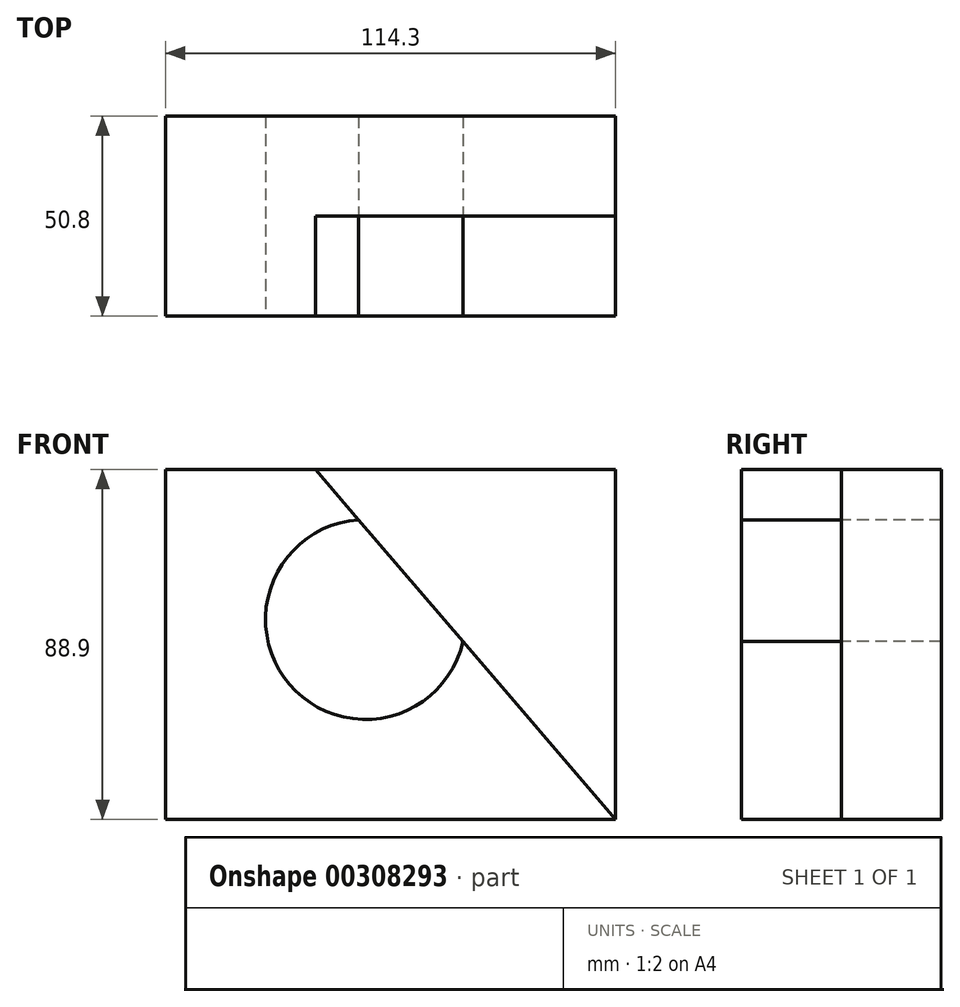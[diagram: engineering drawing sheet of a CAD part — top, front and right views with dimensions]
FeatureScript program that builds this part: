
annotation { "Feature Type Name" : "Feature", "Feature Type Description" : "" }
export const myFeature = defineFeature(function(context is Context, id is Id, definition is map)
    precondition{}
    {
        {
            var Q0;
            Q0=qCreatedBy(makeId("Front.planeOp"),FACE);
            var sketch = newSketch(context, id + "F0", { "sketchPlane" : qUnion([Q0])});
            skLineSegment(sketch, "E0", {"start": v(-57.85, 38.72) * mm, "end": v(-57.85, -50.18) * mm});
            skLineSegment(sketch, "E1", {"start": v(-57.85, -50.18) * mm, "end": v(56.45, -50.18) * mm});
            skLineSegment(sketch, "E2", {"start": v(56.45, -50.18) * mm, "end": v(56.45, 38.72) * mm});
            skLineSegment(sketch, "E3", {"start": v(56.45, 38.72) * mm, "end": v(-57.85, 38.72) * mm});
            skSolve(sketch);
        }
        {
            var Q0;
            Q0=makeQuery(id+"F0.imprint","IMPRINT",FACE,{"disambiguationData":[TD([[makeQuery(id+"F0.imprint","IMPRINT",EDGE,{"derivedFrom":sQuery(id+"F0.wireOp",EDGE,"E0")}),1.0]])]});
            extrude(context, id + "F1", {"entities" : qUnion([Q0]), "depth" : 25.4 * mm});
        }
        {
            var Q0;
            Q0=makeQuery(id+"F1.opExtrude","CAP_FACE",FACE,{"disambiguationData":[OSD([sQuery(id+"F0.wireOp",EDGE,"E0"),sQuery(id+"F0.wireOp",EDGE,"E1"),sQuery(id+"F0.wireOp",EDGE,"E2"),sQuery(id+"F0.wireOp",EDGE,"E3")])],"isStart":false});
            var sketch = newSketch(context, id + "F2", { "sketchPlane" : qUnion([Q0])});
            skLineSegment(sketch, "E4", {"start": v(-57.85, 38.72) * mm, "end": v(-19.75, 38.72) * mm});
            skLineSegment(sketch, "E5", {"start": v(-19.75, 38.72) * mm, "end": v(56.45, -50.18) * mm});
            skSolve(sketch);
        }
        {
            var Q0;
            Q0=makeQuery(id+"F2.imprint","IMPRINT",FACE,{"disambiguationData":[TD([[makeQuery(id+"F2.imprint","IMPRINT",EDGE,{"derivedFrom":sQuery(id+"F2.wireOp",EDGE,"E4")}),1.0]])]});
            extrude(context, id + "F3", {"entities" : qUnion([Q0]), "operationType" : NewBodyOperationType.ADD, "depth" : 25.4 * mm});
        }
        {
            var Q0;
            Q0=makeQuery(id+"F3.opExtrude","CAP_FACE",FACE,{"disambiguationData":[OSD([sQuery(id+"F0.wireOp",EDGE,"E0"),sQuery(id+"F0.wireOp",EDGE,"E1"),sQuery(id+"F2.wireOp",EDGE,"E4"),sQuery(id+"F2.wireOp",EDGE,"E5")])],"isStart":false});
            var sketch = newSketch(context, id + "F4", { "sketchPlane" : qUnion([Q0])});
            skLineSegment(sketch, "E6", {"start": v(-57.85, -50.18) * mm, "end": v(-7.05, -50.18) * mm});
            skLineSegment(sketch, "E7", {"start": v(-7.05, -50.18) * mm, "end": v(-7.05, 23.9) * mm});
            skLineSegment(sketch, "E8", {"start": v(-57.85, -50.18) * mm, "end": v(-57.85, 0.62) * mm});
            skLineSegment(sketch, "E9", {"start": v(-57.85, 0.62) * mm, "end": v(-7.05, 0.62) * mm});
            skCircle(sketch, "E10", {"center": v(-7.05, 0.62) * mm, "radius": 25.4 * mm});
            skSolve(sketch);
        }
        {
            var Q0;
            {var subQ0=sQuery(id+"F4.wireOp",EDGE,"E7");var subQ1=makeQuery(id+"F3.opExtrude","CAP_EDGE",EDGE,{"disambiguationData":[OSD([sQuery(id+"F2.wireOp",EDGE,"E5")])],"isStart":false});var subQ2=makeQuery(id+"F4.imprint","INTERSECT",VERTEX,{"derivedFrom":[subQ1,subQ0]});Q0=makeQuery(id+"F4.imprint","IMPRINT",FACE,{"disambiguationData":[TD([[makeQuery(id+"F4.imprint","IMPRINT",EDGE,{"disambiguationData":[TD([[subQ2,1.0]])],"derivedFrom":subQ0}),1.0]])]});}
            var Q1;
            {var subQ0=sQuery(id+"F4.wireOp",EDGE,"E9");var subQ1=sQuery(id+"F4.wireOp",EDGE,"E7");var subQ2=makeQuery(id+"F4.imprint","INTERSECT",VERTEX,{"derivedFrom":[subQ1,subQ0]});Q1=makeQuery(id+"F4.imprint","IMPRINT",FACE,{"disambiguationData":[TD([[makeQuery(id+"F4.imprint","IMPRINT",EDGE,{"disambiguationData":[TD([[subQ2,1.0]])],"derivedFrom":subQ1}),1.0]])]});}
            var Q2;
            {var subQ0=sQuery(id+"F4.wireOp",EDGE,"E7");var subQ1=makeQuery(id+"F4.imprint","INTERSECT",VERTEX,{"derivedFrom":[subQ0,sQuery(id+"F4.wireOp",EDGE,"E9")]});Q2=makeQuery(id+"F4.imprint","IMPRINT",FACE,{"disambiguationData":[TD([[makeQuery(id+"F4.imprint","IMPRINT",EDGE,{"disambiguationData":[TD([[subQ1,1.0]])],"derivedFrom":subQ0}),-1.0]])]});}
            var Q3;
            {var subQ0=sQuery(id+"F4.wireOp",EDGE,"E10");var subQ1=makeQuery(id+"F3.opExtrude","CAP_EDGE",EDGE,{"disambiguationData":[OSD([sQuery(id+"F2.wireOp",EDGE,"E5")])],"isStart":false});var subQ2=makeQuery(id+"F4.imprint","INTERSECT",VERTEX,{"disambiguationData":[OD(0.0)],"derivedFrom":[subQ1,subQ0]});Q3=makeQuery(id+"F4.imprint","IMPRINT",FACE,{"disambiguationData":[TD([[makeQuery(id+"F4.imprint","IMPRINT",EDGE,{"disambiguationData":[TD([[subQ2,1.0]])],"derivedFrom":subQ0}),1.0]])]});}
            extrude(context, id + "F5", {"entities" : qUnion([Q0, Q1, Q2, Q3]), "operationType" : NewBodyOperationType.REMOVE, "oppositeDirection" : true, "depth" : 50.8 * mm});
        }
    });
